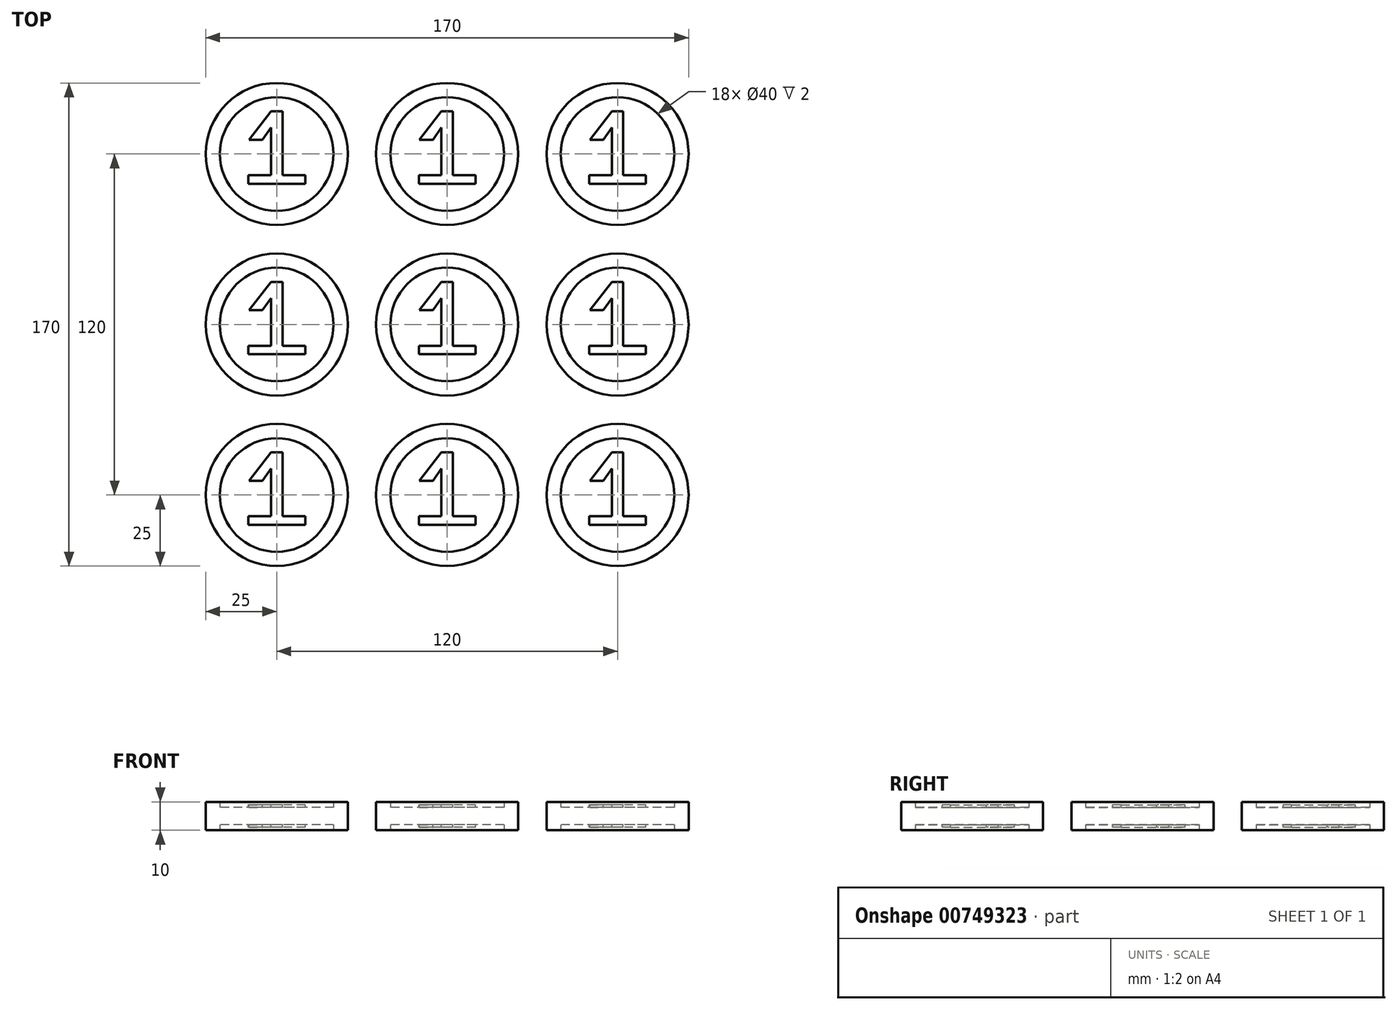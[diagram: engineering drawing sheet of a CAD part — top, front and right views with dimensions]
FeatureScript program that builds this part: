
annotation { "Feature Type Name" : "Feature", "Feature Type Description" : "" }
export const myFeature = defineFeature(function(context is Context, id is Id, definition is map)
    precondition{}
    {
        {
            var Q0;
            Q0=qCreatedBy(makeId("Top.planeOp"),FACE);
            var sketch = newSketch(context, id + "F0", { "sketchPlane" : qUnion([Q0])});
            skCircle(sketch, "E0", {"center": v(0, 0) * mm, "radius": 25 * mm});
            skCircle(sketch, "E1", {"center": v(0, 0) * mm, "radius": 20 * mm});
            skLineSegment(sketch, "E2.bottom", {"start": v(10, -7.5) * mm, "end": v(-10, -7.5) * mm});
            skLineSegment(sketch, "E2.top", {"start": v(10, -10.5) * mm, "end": v(-10, -10.5) * mm});
            skLineSegment(sketch, "E2.left", {"start": v(10, -7.5) * mm, "end": v(10, -10.5) * mm});
            skLineSegment(sketch, "E2.right", {"start": v(-10, -7.5) * mm, "end": v(-10, -10.5) * mm});
            skLineSegment(sketch, "E3.bottom", {"start": v(2, -10.5) * mm, "end": v(-2, -10.5) * mm});
            skLineSegment(sketch, "E3.top", {"start": v(2, 15) * mm, "end": v(-2, 15) * mm});
            skLineSegment(sketch, "E3.left", {"start": v(2, -10.5) * mm, "end": v(2, 15) * mm});
            skLineSegment(sketch, "E3.right", {"start": v(-2, -10.5) * mm, "end": v(-2, 15) * mm});
            skLineSegment(sketch, "E4", {"start": v(-2, 15) * mm, "end": v(-9.78, 5) * mm});
            skLineSegment(sketch, "E5", {"start": v(-9.78, 5) * mm, "end": v(-5, 5) * mm});
            skLineSegment(sketch, "E6", {"start": v(2, 15) * mm, "end": v(-5, 5) * mm});
            skSolve(sketch);
        }
        {
            var Q0;
            Q0=makeQuery(id+"F0.imprint","IMPRINT",FACE,{"disambiguationData":[TD([[makeQuery(id+"F0.imprint","IMPRINT",EDGE,{"derivedFrom":sQuery(id+"F0.wireOp",EDGE,"E0")}),1.0]])]});
            extrude(context, id + "F1", {"entities" : qUnion([Q0]), "endBound" : BoundingType.SYMMETRIC, "depth" : 10 * mm, "offsetDistance" : 25.4 * mm});
        }
        {
            var Q0;
            Q0=makeQuery(id+"F0.imprint","IMPRINT",FACE,{"disambiguationData":[TD([[makeQuery(id+"F0.imprint","IMPRINT",EDGE,{"derivedFrom":sQuery(id+"F0.wireOp",EDGE,"E1")}),1.0]])]});
            extrude(context, id + "F2", {"entities" : qUnion([Q0]), "operationType" : NewBodyOperationType.ADD, "endBound" : BoundingType.SYMMETRIC, "depth" : 6 * mm, "offsetDistance" : 25.4 * mm});
        }
        {
            var Q0;
            {var subQ0=sQuery(id+"F0.wireOp",EDGE,"nvZ7VyVJ-02HF-v250-04MJ-ALM832vaFEjy");Q0=makeQuery(id+"F0.imprint","IMPRINT",FACE,{"disambiguationData":[TD([[makeQuery(id+"F0.imprint","IMPRINT",EDGE,{"derivedFrom":subQ0}),-1.0]])]});}
            var Q1;
            {var subQ4=sQuery(id+"F0.wireOp",EDGE,"g6EXFdHc-cWUs-hhlX-nSIb-98dc7lWUQFuj");Q1=makeQuery(id+"F0.imprint","IMPRINT",FACE,{"disambiguationData":[TD([[makeQuery(id+"F0.imprint","IMPRINT",EDGE,{"derivedFrom":subQ4}),-1.0]])]});}
            var Q2;
            {var subQ1=sQuery(id+"F0.wireOp",EDGE,"w6P6AIPZ-1UnD-HAA8-nrUS-kuMTXG8RY9wD");var subQ3=sQuery(id+"F0.wireOp",EDGE,"xZKMv0bG-1cml-miL5-5VcU-VNFomGCGhqUf");var subQ4=makeQuery(id+"F0.imprint","INTERSECT",VERTEX,{"derivedFrom":[subQ1,subQ3]});Q2=makeQuery(id+"F0.imprint","IMPRINT",FACE,{"disambiguationData":[TD([[makeQuery(id+"F0.imprint","IMPRINT",EDGE,{"disambiguationData":[TD([[subQ4,-1.0]])],"derivedFrom":subQ3}),1.0]])]});}
            var Q3;
            {var subQ0=sQuery(id+"F0.wireOp",EDGE,"xNTKOAnv-Cnho-LKE1-hlHZ-S8kQni3QPAZu");Q3=makeQuery(id+"F0.imprint","IMPRINT",FACE,{"disambiguationData":[TD([[makeQuery(id+"F0.imprint","IMPRINT",EDGE,{"derivedFrom":subQ0}),-1.0]])]});}
            var Q4;
            {var subQ0=sQuery(id+"F0.wireOp",EDGE,"F5pbwe9F-0fm2-K3Xc-wWsB-O6E6BB2tMhNi");Q4=makeQuery(id+"F0.imprint","IMPRINT",FACE,{"disambiguationData":[TD([[makeQuery(id+"F0.imprint","IMPRINT",EDGE,{"derivedFrom":subQ0}),-1.0]])]});}
            var Q5;
            {var subQ0=sQuery(id+"F0.wireOp",EDGE,"YgFhtI2o-0aZ2-URYS-eqmX-a6Np0ajwhMmC");Q5=makeQuery(id+"F0.imprint","IMPRINT",FACE,{"disambiguationData":[TD([[makeQuery(id+"F0.imprint","IMPRINT",EDGE,{"derivedFrom":subQ0}),-1.0]])]});}
            var Q6;
            {var subQ3=sQuery(id+"F0.wireOp",EDGE,"E2.right");Q6=makeQuery(id+"F0.imprint","IMPRINT",FACE,{"disambiguationData":[TD([[makeQuery(id+"F0.imprint","IMPRINT",EDGE,{"derivedFrom":subQ3}),1.0]])]});}
            var Q7;
            {var subQ0=sQuery(id+"F0.wireOp",EDGE,"E3.right");var subQ1=sQuery(id+"F0.wireOp",EDGE,"E2.bottom");var subQ2=makeQuery(id+"F0.imprint","INTERSECT",VERTEX,{"derivedFrom":[subQ1,subQ0]});Q7=makeQuery(id+"F0.imprint","IMPRINT",FACE,{"disambiguationData":[TD([[makeQuery(id+"F0.imprint","IMPRINT",EDGE,{"disambiguationData":[TD([[subQ2,1.0]])],"derivedFrom":subQ1}),1.0]])]});}
            var Q8;
            {var subQ0=sQuery(id+"F0.wireOp",EDGE,"E2.left");Q8=makeQuery(id+"F0.imprint","IMPRINT",FACE,{"disambiguationData":[TD([[makeQuery(id+"F0.imprint","IMPRINT",EDGE,{"derivedFrom":subQ0}),-1.0]])]});}
            var Q9;
            {var subQ0=sQuery(id+"F0.wireOp",EDGE,"E4");Q9=makeQuery(id+"F0.imprint","IMPRINT",FACE,{"disambiguationData":[TD([[makeQuery(id+"F0.imprint","IMPRINT",EDGE,{"derivedFrom":subQ0}),1.0]])]});}
            var Q10;
            {var subQ0=sQuery(id+"F0.wireOp",EDGE,"E3.right");var subQ1=sQuery(id+"F0.wireOp",EDGE,"E2.bottom");var subQ2=makeQuery(id+"F0.imprint","INTERSECT",VERTEX,{"derivedFrom":[subQ1,subQ0]});Q10=makeQuery(id+"F0.imprint","IMPRINT",FACE,{"disambiguationData":[TD([[makeQuery(id+"F0.imprint","IMPRINT",EDGE,{"disambiguationData":[TD([[subQ2,1.0]])],"derivedFrom":subQ1}),-1.0]])]});}
            var Q11;
            {var subQ0=sQuery(id+"F0.wireOp",EDGE,"E3.top");Q11=makeQuery(id+"F0.imprint","IMPRINT",FACE,{"disambiguationData":[TD([[makeQuery(id+"F0.imprint","IMPRINT",EDGE,{"derivedFrom":subQ0}),1.0]])]});}
            extrude(context, id + "F3", {"entities" : qUnion([Q0, Q1, Q2, Q3, Q4, Q5, Q6, Q7, Q8, Q9, Q10, Q11]), "operationType" : NewBodyOperationType.ADD, "endBound" : BoundingType.SYMMETRIC, "oppositeDirection" : true, "depth" : 8 * mm, "offsetDistance" : 25.4 * mm});
        }
        {
            var Q0;
            Q0=makeQuery(id+"F1.opExtrude","SWEPT_BODY",BODY,{"disambiguationData":[OSD([sQuery(id+"F0.wireOp",EDGE,"E0"),sQuery(id+"F0.wireOp",EDGE,"E1")])]});
            transform(context, id + "F4", {"entities" : qUnion([Q0]), "transformType" : TransformType.TRANSLATION_3D, "dx" : 60 * mm, "dy" : 0 * mm, "dz" : 0 * mm, "makeCopy" : true});
        }
        {
            var Q0;
            Q0=makeQuery(id+"F1.opExtrude","SWEPT_BODY",BODY,{"disambiguationData":[OSD([sQuery(id+"F0.wireOp",EDGE,"E0"),sQuery(id+"F0.wireOp",EDGE,"E1")])]});
            transform(context, id + "F5", {"entities" : qUnion([Q0]), "transformType" : TransformType.TRANSLATION_3D, "dx" : -60 * mm, "dy" : 0 * mm, "dz" : 0 * mm, "makeCopy" : true});
        }
        {
            var Q0;
            Q0=makeQuery(id+"F1.opExtrude","SWEPT_BODY",BODY,{"disambiguationData":[OSD([sQuery(id+"F0.wireOp",EDGE,"E0"),sQuery(id+"F0.wireOp",EDGE,"E1")])]});
            transform(context, id + "F6", {"entities" : qUnion([Q0]), "transformType" : TransformType.TRANSLATION_3D, "dx" : -60 * mm, "dy" : 60 * mm, "dz" : 0 * mm, "makeCopy" : true});
        }
        {
            var Q0;
            Q0=makeQuery(id+"F1.opExtrude","SWEPT_BODY",BODY,{"disambiguationData":[OSD([sQuery(id+"F0.wireOp",EDGE,"E0"),sQuery(id+"F0.wireOp",EDGE,"E1")])]});
            transform(context, id + "F7", {"entities" : qUnion([Q0]), "transformType" : TransformType.TRANSLATION_3D, "dx" : 0 * mm, "dy" : 60 * mm, "dz" : 0 * mm, "makeCopy" : true});
        }
        {
            var Q0;
            Q0=makeQuery(id+"F1.opExtrude","SWEPT_BODY",BODY,{"disambiguationData":[OSD([sQuery(id+"F0.wireOp",EDGE,"E0"),sQuery(id+"F0.wireOp",EDGE,"E1")])]});
            transform(context, id + "F8", {"entities" : qUnion([Q0]), "transformType" : TransformType.TRANSLATION_3D, "dx" : 60 * mm, "dy" : 60 * mm, "dz" : 0 * mm, "makeCopy" : true});
        }
        {
            var Q0;
            Q0=makeQuery(id+"F1.opExtrude","SWEPT_BODY",BODY,{"disambiguationData":[OSD([sQuery(id+"F0.wireOp",EDGE,"E0"),sQuery(id+"F0.wireOp",EDGE,"E1")])]});
            transform(context, id + "F9", {"entities" : qUnion([Q0]), "transformType" : TransformType.TRANSLATION_3D, "dx" : 60 * mm, "dy" : -60 * mm, "dz" : 0 * mm, "makeCopy" : true});
        }
        {
            var Q0;
            Q0=makeQuery(id+"F1.opExtrude","SWEPT_BODY",BODY,{"disambiguationData":[OSD([sQuery(id+"F0.wireOp",EDGE,"E0"),sQuery(id+"F0.wireOp",EDGE,"E1")])]});
            transform(context, id + "F10", {"entities" : qUnion([Q0]), "transformType" : TransformType.TRANSLATION_3D, "dx" : 0 * mm, "dy" : -60 * mm, "dz" : 0 * mm, "makeCopy" : true});
        }
        {
            var Q0;
            Q0=makeQuery(id+"F1.opExtrude","SWEPT_BODY",BODY,{"disambiguationData":[OSD([sQuery(id+"F0.wireOp",EDGE,"E0"),sQuery(id+"F0.wireOp",EDGE,"E1")])]});
            transform(context, id + "F11", {"entities" : qUnion([Q0]), "transformType" : TransformType.TRANSLATION_3D, "dx" : -60 * mm, "dy" : -60 * mm, "dz" : 0 * mm, "makeCopy" : true});
        }
    });
